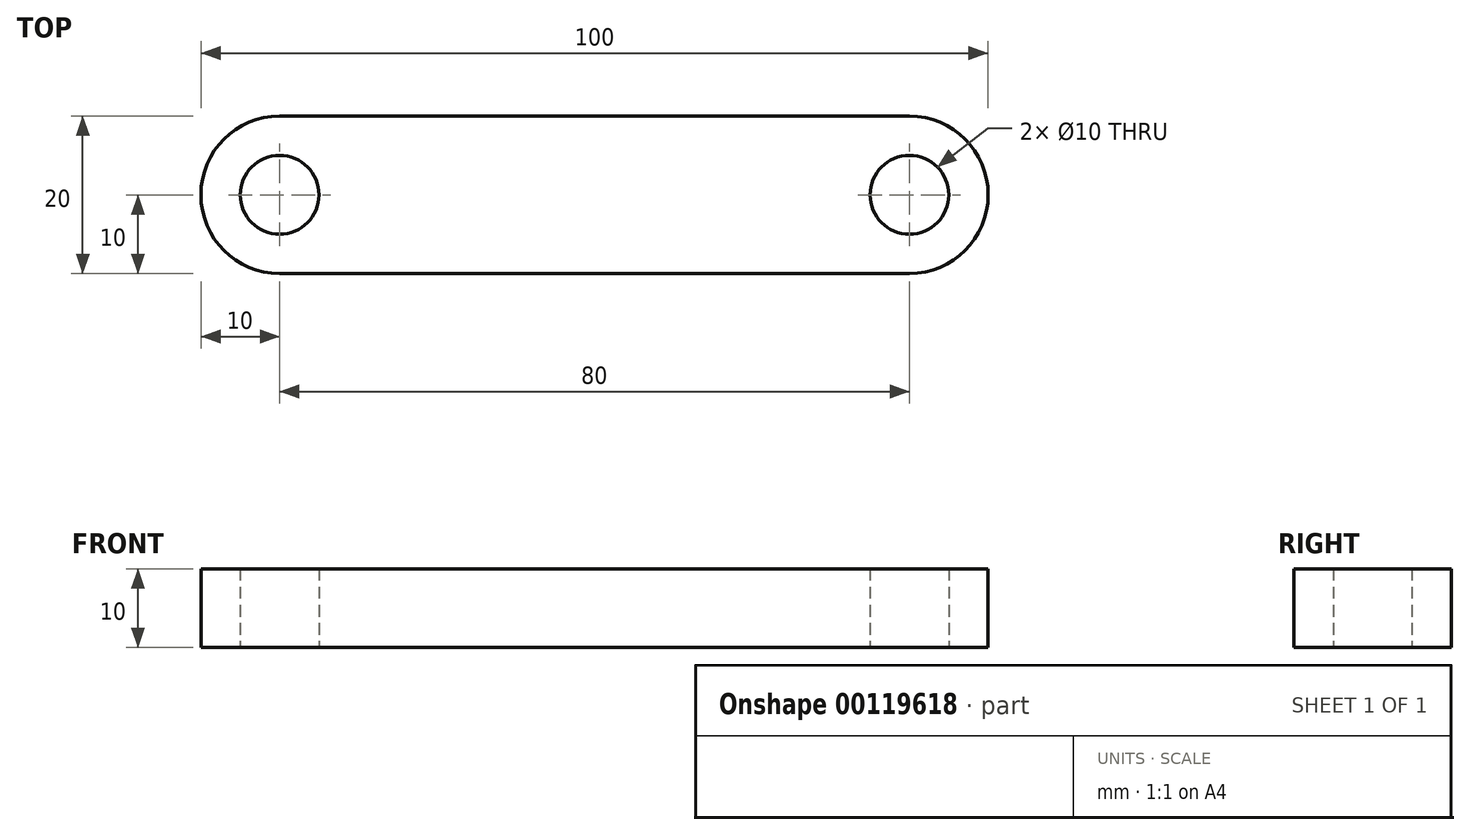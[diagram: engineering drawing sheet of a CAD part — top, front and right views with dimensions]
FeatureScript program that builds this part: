
annotation { "Feature Type Name" : "Feature", "Feature Type Description" : "" }
export const myFeature = defineFeature(function(context is Context, id is Id, definition is map)
    precondition{}
    {
        {
            var Q0;
            Q0=qCreatedBy(makeId("Top.planeOp"),FACE);
            var sketch = newSketch(context, id + "F0", { "sketchPlane" : qUnion([Q0])});
            skArc(sketch, "E0", {"start": v(-40, 10) * mm, "mid": v(-50, 0) * mm, "end": v(-40, -10) * mm});
            skArc(sketch, "E1", {"start": v(40, -10) * mm, "mid": v(50, 0) * mm, "end": v(40, 10) * mm});
            skLineSegment(sketch, "E2", {"start": v(-40, 10) * mm, "end": v(40, 10) * mm});
            skLineSegment(sketch, "E3", {"start": v(-40, -10) * mm, "end": v(40, -10) * mm});
            skCircle(sketch, "E4", {"center": v(-40, 0) * mm, "radius": 5 * mm});
            skCircle(sketch, "E5", {"center": v(40, 0) * mm, "radius": 5 * mm});
            skSolve(sketch);
        }
        {
            var Q0;
            Q0 = qSketchRegion(id + "F0", true);
            extrude(context, id + "F1", {"entities" : qUnion([Q0]), "depth" : 10 * mm});
        }
    });
